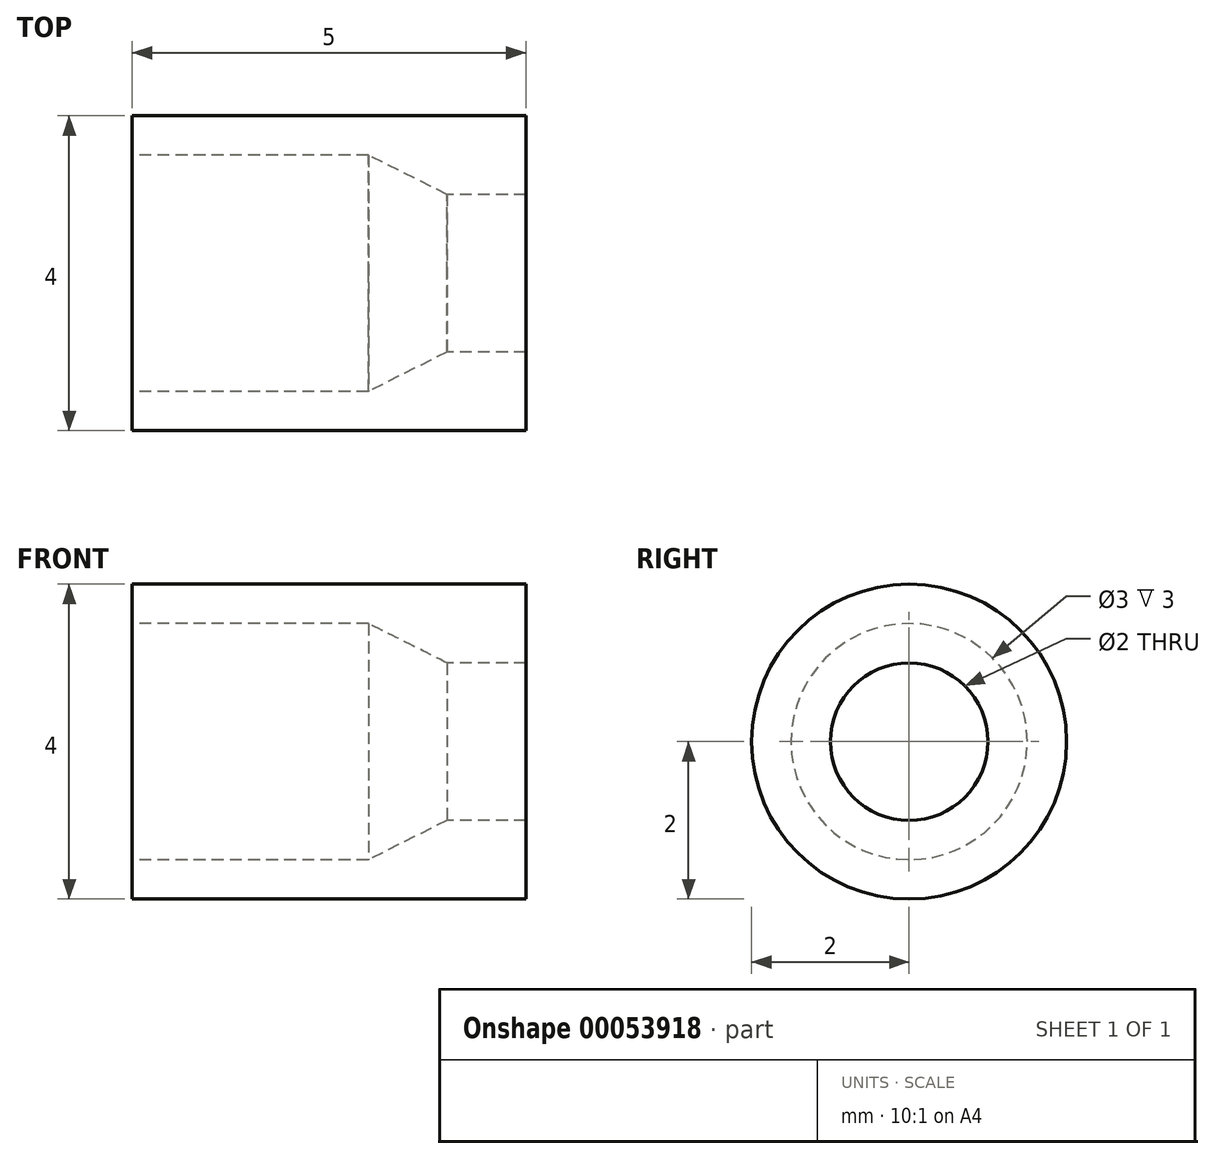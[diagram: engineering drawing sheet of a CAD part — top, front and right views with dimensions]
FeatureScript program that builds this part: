
annotation { "Feature Type Name" : "Feature", "Feature Type Description" : "" }
export const myFeature = defineFeature(function(context is Context, id is Id, definition is map)
    precondition{}
    {
        {
            var Q0;
            Q0=qCreatedBy(makeId("Front.planeOp"),FACE);
            var sketch = newSketch(context, id + "F0", { "sketchPlane" : qUnion([Q0])});
            skLineSegment(sketch, "E0", {"start": v(0, 0) * mm, "end": v(0, 2) * mm});
            skLineSegment(sketch, "E1", {"start": v(0, 2) * mm, "end": v(5, 2) * mm});
            skLineSegment(sketch, "E2", {"start": v(5, 2) * mm, "end": v(5, 1) * mm});
            skLineSegment(sketch, "E3", {"start": v(5, 1) * mm, "end": v(4, 1) * mm});
            skLineSegment(sketch, "E4", {"start": v(4, 1) * mm, "end": v(3, 1.5) * mm});
            skLineSegment(sketch, "E5", {"start": v(3, 1.5) * mm, "end": v(0, 1.5) * mm});
            skLineSegment(sketch, "E6", {"start": v(0, 0) * mm, "end": v(5, 0) * mm});
            skLineSegment(sketch, "E7", {"start": v(5, 0) * mm, "end": v(5, 1) * mm});
            skSolve(sketch);
        }
        {
            var Q0;
            {var subQ0=sQuery(id+"F0.wireOp",EDGE,"E1");Q0=makeQuery(id+"F0.imprint","IMPRINT",FACE,{"disambiguationData":[TD([[makeQuery(id+"F0.imprint","IMPRINT",EDGE,{"derivedFrom":subQ0}),-1.0]])]});}
            var Q1;
            Q1=sQuery(id+"F0.wireOp",EDGE,"E6");
            revolve(context, id + "F1", {"entities" : qUnion([Q0]), "axis" : qUnion([Q1]), "revolveType" : RevolveType.FULL});
        }
    });
